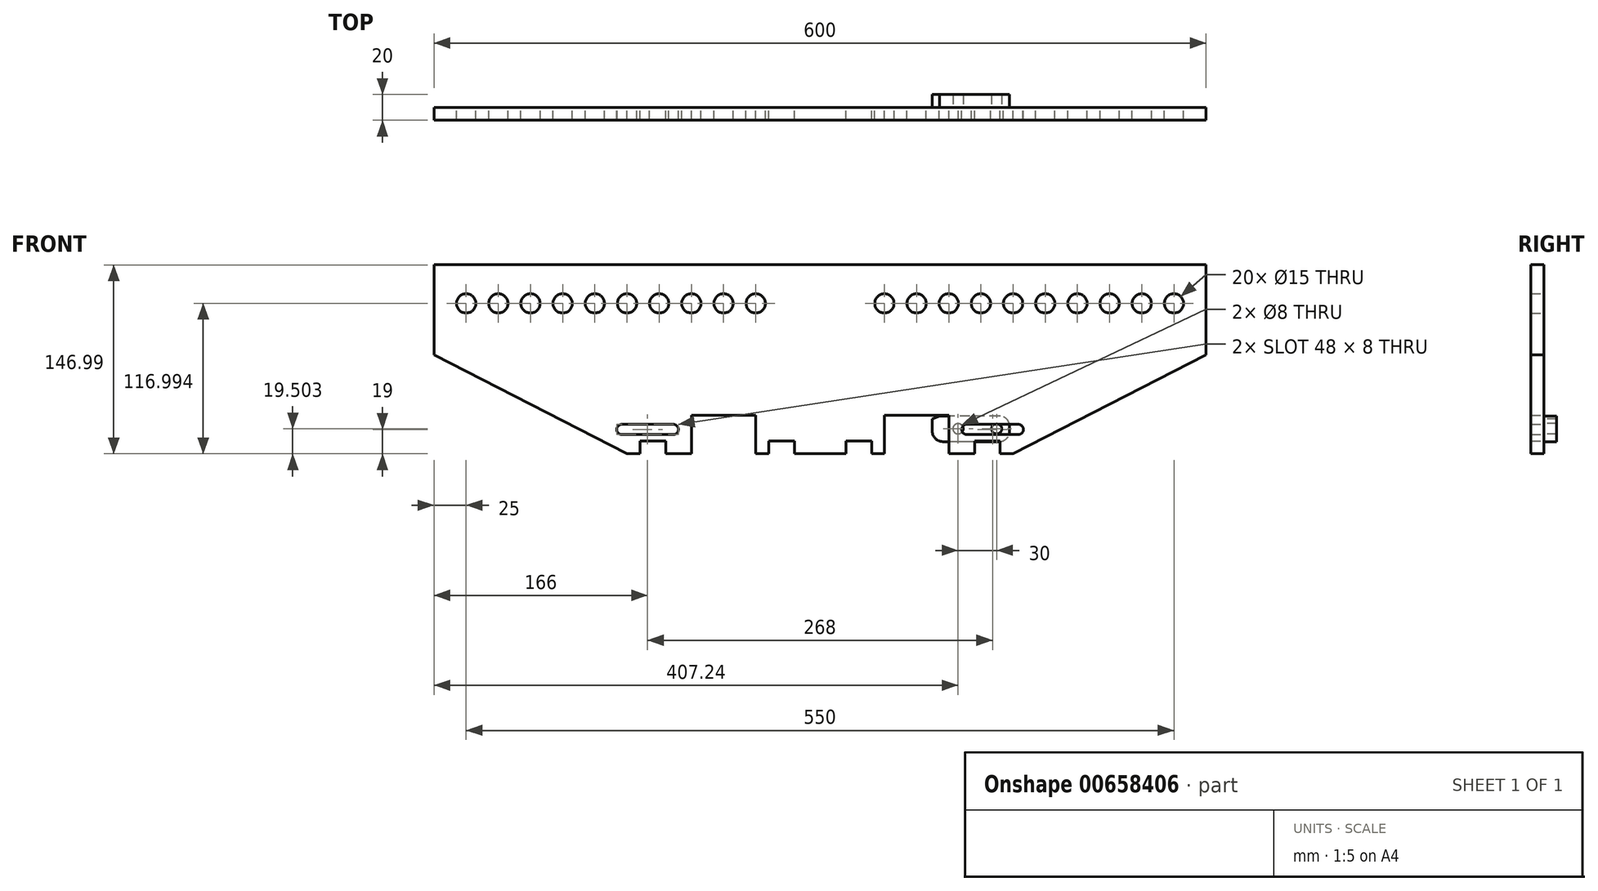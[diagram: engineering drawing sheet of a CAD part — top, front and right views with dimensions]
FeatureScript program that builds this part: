
annotation { "Feature Type Name" : "Feature", "Feature Type Description" : "" }
export const myFeature = defineFeature(function(context is Context, id is Id, definition is map)
    precondition{}
    {
        {
            var Q0;
            Q0=qCreatedBy(makeId("Front.planeOp"),FACE);
            var sketch = newSketch(context, id + "F0", { "sketchPlane" : qUnion([Q0])});
            skLineSegment(sketch, "E0", {"start": v(0, 0) * mm, "end": v(20, 0) * mm});
            skLineSegment(sketch, "E1", {"start": v(50, 0) * mm, "end": v(50, 30) * mm});
            skLineSegment(sketch, "E2", {"start": v(50, 30) * mm, "end": v(100, 30) * mm});
            skLineSegment(sketch, "E3", {"start": v(100, 30) * mm, "end": v(100, 0) * mm});
            skLineSegment(sketch, "E4", {"start": v(100, 0) * mm, "end": v(120, 0) * mm});
            skLineSegment(sketch, "E5", {"start": v(150, 0) * mm, "end": v(300, 77) * mm});
            skLineSegment(sketch, "E6", {"start": v(300, 77) * mm, "end": v(300, 147) * mm});
            skLineSegment(sketch, "E7", {"start": v(300, 147) * mm, "end": v(0, 147) * mm});
            skLineSegment(sketch, "E8", {"start": v(0, 173.35) * mm, "end": v(0, -36.55) * mm, "construction": true});
            skCircle(sketch, "E9", {"center": v(50, 117) * mm, "radius": 7.5 * mm});
            skCircle(sketch, "E10.1.0.0", {"center": v(75, 117) * mm, "radius": 7.5 * mm});
            skCircle(sketch, "E10.2.0.0", {"center": v(100, 117) * mm, "radius": 7.5 * mm});
            skCircle(sketch, "E10.3.0.0", {"center": v(125, 117) * mm, "radius": 7.5 * mm});
            skCircle(sketch, "E10.4.0.0", {"center": v(150, 117) * mm, "radius": 7.5 * mm});
            skCircle(sketch, "E10.5.0.0", {"center": v(175, 117) * mm, "radius": 7.5 * mm});
            skCircle(sketch, "E10.6.0.0", {"center": v(200, 117) * mm, "radius": 7.5 * mm});
            skCircle(sketch, "E10.7.0.0", {"center": v(225, 117) * mm, "radius": 7.5 * mm});
            skCircle(sketch, "E10.8.0.0", {"center": v(250, 117) * mm, "radius": 7.5 * mm});
            skCircle(sketch, "E10.9.0.0", {"center": v(275, 117) * mm, "radius": 7.5 * mm});
            skLineSegment(sketch, "E10.direction1", {"start": v(50, 117) * mm, "end": v(75, 117) * mm, "construction": true});
            skLineSegment(sketch, "E11.MirrorCS", {"start": v(-50, 0) * mm, "end": v(-50, 30) * mm});
            skCircle(sketch, "E12.MirrorC", {"center": v(-225, 117) * mm, "radius": 7.5 * mm});
            skCircle(sketch, "E13.MirrorC", {"center": v(-275, 117) * mm, "radius": 7.5 * mm});
            skCircle(sketch, "E14.MirrorC", {"center": v(-175, 117) * mm, "radius": 7.5 * mm});
            skLineSegment(sketch, "E15.MirrorCS", {"start": v(-100, 30) * mm, "end": v(-100, 0) * mm});
            skLineSegment(sketch, "E16.MirrorCS", {"start": v(-50, 30) * mm, "end": v(-100, 30) * mm});
            skLineSegment(sketch, "E17.MirrorCS", {"start": v(-100, 0) * mm, "end": v(-120, 0) * mm});
            skLineSegment(sketch, "E18.MirrorCS", {"start": v(-300, 77) * mm, "end": v(-300, 147) * mm});
            skLineSegment(sketch, "E19.MirrorCS", {"start": v(-300, 147) * mm, "end": v(0, 147) * mm});
            skLineSegment(sketch, "E20.MirrorCS", {"start": v(-50, 117) * mm, "end": v(-75, 117) * mm, "construction": true});
            skCircle(sketch, "E21.MirrorC", {"center": v(-50, 117) * mm, "radius": 7.5 * mm});
            skLineSegment(sketch, "E22.MirrorCS", {"start": v(0, 0) * mm, "end": v(-20, 0) * mm});
            skCircle(sketch, "E23.MirrorC", {"center": v(-125, 117) * mm, "radius": 7.5 * mm});
            skCircle(sketch, "E24.MirrorC", {"center": v(-100, 117) * mm, "radius": 7.5 * mm});
            skCircle(sketch, "E25.MirrorC", {"center": v(-150, 117) * mm, "radius": 7.5 * mm});
            skCircle(sketch, "E26.MirrorC", {"center": v(-250, 117) * mm, "radius": 7.5 * mm});
            skLineSegment(sketch, "E27.MirrorCS", {"start": v(-150, 0) * mm, "end": v(-300, 77) * mm});
            skCircle(sketch, "E28.MirrorC", {"center": v(-200, 117) * mm, "radius": 7.5 * mm});
            skCircle(sketch, "E29.MirrorC", {"center": v(-75, 117) * mm, "radius": 7.5 * mm});
            skLineSegment(sketch, "E30.bottom", {"start": v(154, 23) * mm, "end": v(114, 23) * mm});
            skLineSegment(sketch, "E30.top", {"start": v(154, 15) * mm, "end": v(114, 15) * mm});
            skArc(sketch, "E31", {"start": v(154, 15) * mm, "mid": v(158, 19) * mm, "end": v(154, 23) * mm});
            skArc(sketch, "E32", {"start": v(114, 23) * mm, "mid": v(110, 19) * mm, "end": v(114, 15) * mm});
            skArc(sketch, "E33.MirrorCS", {"start": v(-154, 15) * mm, "mid": v(-158, 19) * mm, "end": v(-154, 23) * mm});
            skArc(sketch, "E34.MirrorCS", {"start": v(-114, 23) * mm, "mid": v(-110, 19) * mm, "end": v(-114, 15) * mm});
            skLineSegment(sketch, "E35.MirrorCS", {"start": v(-154, 15) * mm, "end": v(-114, 15) * mm});
            skLineSegment(sketch, "E36.MirrorCS", {"start": v(-154, 23) * mm, "end": v(-114, 23) * mm});
            skLineSegment(sketch, "E37", {"start": v(140, 0) * mm, "end": v(140, 10) * mm});
            skLineSegment(sketch, "E38", {"start": v(140, 10) * mm, "end": v(120, 10) * mm});
            skLineSegment(sketch, "E39", {"start": v(120, 10) * mm, "end": v(120, 0) * mm});
            skLineSegment(sketch, "E40.trimOffspring", {"start": v(140, 0) * mm, "end": v(150, 0) * mm});
            skLineSegment(sketch, "E41.MirrorCS", {"start": v(-120, 10) * mm, "end": v(-120, 0) * mm});
            skLineSegment(sketch, "E42.MirrorCS", {"start": v(-140, 10) * mm, "end": v(-120, 10) * mm});
            skLineSegment(sketch, "E43.MirrorCS", {"start": v(-140, 0) * mm, "end": v(-140, 10) * mm});
            skLineSegment(sketch, "E44.trimOffspring", {"start": v(-140, 0) * mm, "end": v(-150, 0) * mm});
            skLineSegment(sketch, "E45", {"start": v(40, 0) * mm, "end": v(40, 10) * mm});
            skLineSegment(sketch, "E46", {"start": v(40, 10) * mm, "end": v(20, 10) * mm});
            skLineSegment(sketch, "E47", {"start": v(20, 10) * mm, "end": v(20, 0) * mm});
            skLineSegment(sketch, "E48.trimOffspring", {"start": v(40, 0) * mm, "end": v(50, 0) * mm});
            skLineSegment(sketch, "E49.MirrorCS", {"start": v(-40, 0) * mm, "end": v(-40, 10) * mm});
            skLineSegment(sketch, "E50.MirrorCS", {"start": v(-40, 10) * mm, "end": v(-20, 10) * mm});
            skLineSegment(sketch, "E51.MirrorCS", {"start": v(-20, 10) * mm, "end": v(-20, 0) * mm});
            skLineSegment(sketch, "E52.trimOffspring", {"start": v(-40, 0) * mm, "end": v(-50, 0) * mm});
            skSolve(sketch);
        }
        {
            var Q0;
            Q0=makeQuery(id+"F0.imprint","IMPRINT",FACE,{"disambiguationData":[TD([[makeQuery(id+"F0.imprint","IMPRINT",EDGE,{"derivedFrom":sQuery(id+"F0.wireOp",EDGE,"E0")}),1.0]])]});
            extrude(context, id + "F1", {"entities" : qUnion([Q0]), "depth" : 10 * mm, "offsetDistance" : 25 * mm});
        }
        {
            var Q0;
            Q0=makeQuery(id+"F1.opExtrude","CAP_FACE",FACE,{"disambiguationData":[OSD([sQuery(id+"F0.wireOp",EDGE,"E0"),sQuery(id+"F0.wireOp",EDGE,"E1"),sQuery(id+"F0.wireOp",EDGE,"E2"),sQuery(id+"F0.wireOp",EDGE,"E3"),sQuery(id+"F0.wireOp",EDGE,"E4"),sQuery(id+"F0.wireOp",EDGE,"E5"),sQuery(id+"F0.wireOp",EDGE,"E6"),sQuery(id+"F0.wireOp",EDGE,"E7"),sQuery(id+"F0.wireOp",EDGE,"E9"),sQuery(id+"F0.wireOp",EDGE,"E10.1.0.0"),sQuery(id+"F0.wireOp",EDGE,"E10.2.0.0"),sQuery(id+"F0.wireOp",EDGE,"E10.3.0.0"),sQuery(id+"F0.wireOp",EDGE,"E10.4.0.0"),sQuery(id+"F0.wireOp",EDGE,"E10.5.0.0"),sQuery(id+"F0.wireOp",EDGE,"E10.6.0.0"),sQuery(id+"F0.wireOp",EDGE,"E10.7.0.0"),sQuery(id+"F0.wireOp",EDGE,"E10.8.0.0"),sQuery(id+"F0.wireOp",EDGE,"E10.9.0.0"),sQuery(id+"F0.wireOp",EDGE,"E11.MirrorCS"),sQuery(id+"F0.wireOp",EDGE,"E12.MirrorC"),sQuery(id+"F0.wireOp",EDGE,"E13.MirrorC"),sQuery(id+"F0.wireOp",EDGE,"E14.MirrorC"),sQuery(id+"F0.wireOp",EDGE,"E15.MirrorCS"),sQuery(id+"F0.wireOp",EDGE,"E16.MirrorCS"),sQuery(id+"F0.wireOp",EDGE,"E17.MirrorCS"),sQuery(id+"F0.wireOp",EDGE,"E18.MirrorCS"),sQuery(id+"F0.wireOp",EDGE,"E19.MirrorCS"),sQuery(id+"F0.wireOp",EDGE,"E21.MirrorC"),sQuery(id+"F0.wireOp",EDGE,"E22.MirrorCS"),sQuery(id+"F0.wireOp",EDGE,"E23.MirrorC"),sQuery(id+"F0.wireOp",EDGE,"E24.MirrorC"),sQuery(id+"F0.wireOp",EDGE,"E25.MirrorC"),sQuery(id+"F0.wireOp",EDGE,"E26.MirrorC"),sQuery(id+"F0.wireOp",EDGE,"E27.MirrorCS"),sQuery(id+"F0.wireOp",EDGE,"E28.MirrorC"),sQuery(id+"F0.wireOp",EDGE,"E29.MirrorC"),sQuery(id+"F0.wireOp",EDGE,"E30.bottom"),sQuery(id+"F0.wireOp",EDGE,"E30.top"),sQuery(id+"F0.wireOp",EDGE,"E31"),sQuery(id+"F0.wireOp",EDGE,"E32"),sQuery(id+"F0.wireOp",EDGE,"E33.MirrorCS"),sQuery(id+"F0.wireOp",EDGE,"E34.MirrorCS"),sQuery(id+"F0.wireOp",EDGE,"E35.MirrorCS"),sQuery(id+"F0.wireOp",EDGE,"E36.MirrorCS"),sQuery(id+"F0.wireOp",EDGE,"E37"),sQuery(id+"F0.wireOp",EDGE,"E38"),sQuery(id+"F0.wireOp",EDGE,"E39"),sQuery(id+"F0.wireOp",EDGE,"E40.trimOffspring"),sQuery(id+"F0.wireOp",EDGE,"E41.MirrorCS"),sQuery(id+"F0.wireOp",EDGE,"E42.MirrorCS"),sQuery(id+"F0.wireOp",EDGE,"E43.MirrorCS"),sQuery(id+"F0.wireOp",EDGE,"E44.trimOffspring"),sQuery(id+"F0.wireOp",EDGE,"E45"),sQuery(id+"F0.wireOp",EDGE,"E46"),sQuery(id+"F0.wireOp",EDGE,"E47"),sQuery(id+"F0.wireOp",EDGE,"E48.trimOffspring"),sQuery(id+"F0.wireOp",EDGE,"E49.MirrorCS"),sQuery(id+"F0.wireOp",EDGE,"E50.MirrorCS"),sQuery(id+"F0.wireOp",EDGE,"E51.MirrorCS"),sQuery(id+"F0.wireOp",EDGE,"E52.trimOffspring")])],"isStart":true});
            var sketch = newSketch(context, id + "F2", { "sketchPlane" : qUnion([Q0])});
            skLineSegment(sketch, "E53.bottom", {"start": v(-147.24, 29.5) * mm, "end": v(-93, 29.5) * mm});
            skLineSegment(sketch, "E53.top", {"start": v(-147.24, 9.5) * mm, "end": v(-87.24, 9.5) * mm});
            skLineSegment(sketch, "E53.left", {"start": v(-147.24, 29.5) * mm, "end": v(-147.24, 9.5) * mm});
            skLineSegment(sketch, "E53.right", {"start": v(-87.24, 27.15) * mm, "end": v(-87.24, 9.5) * mm});
            skLineSegment(sketch, "E54", {"start": v(-87.24, 27.15) * mm, "end": v(-93, 29.5) * mm});
            skCircle(sketch, "E55", {"center": v(-137.24, 19.5) * mm, "radius": 4 * mm});
            skPoint(sketch, "E55.centerSnap0", {"position": v(-147.24, 19.5) * mm});
            skCircle(sketch, "E56", {"center": v(-107.24, 19.5) * mm, "radius": 4 * mm});
            skSolve(sketch);
        }
        {
            var Q0;
            Q0 = qSketchRegion(id + "F2", true);
            extrude(context, id + "F3", {"entities" : qUnion([Q0]), "depth" : 10 * mm, "offsetDistance" : 25 * mm});
        }
        {
            var Q0;
            Q0=makeQuery(id+"F3.opExtrude","SWEPT_EDGE",EDGE,{"disambiguationData":[OSD([sQuery(id+"F2.wireOp",EDGE,"E53.bottom"),sQuery(id+"F2.wireOp",EDGE,"E53.left")])]});
            var Q1;
            Q1=makeQuery(id+"F3.opExtrude","SWEPT_EDGE",EDGE,{"disambiguationData":[OSD([sQuery(id+"F2.wireOp",EDGE,"E53.top"),sQuery(id+"F2.wireOp",EDGE,"E53.left")])]});
            var Q2;
            Q2=makeQuery(id+"F3.opExtrude","SWEPT_EDGE",EDGE,{"disambiguationData":[OSD([sQuery(id+"F2.wireOp",EDGE,"E53.top"),sQuery(id+"F2.wireOp",EDGE,"E53.right")])]});
            fillet(context, id + "F4", {"entities" : qUnion([Q0, Q1, Q2]), "radius" : 8 * mm, "tangentPropagation" : true, "allowEdgeOverflow" : false});
        }
    });
